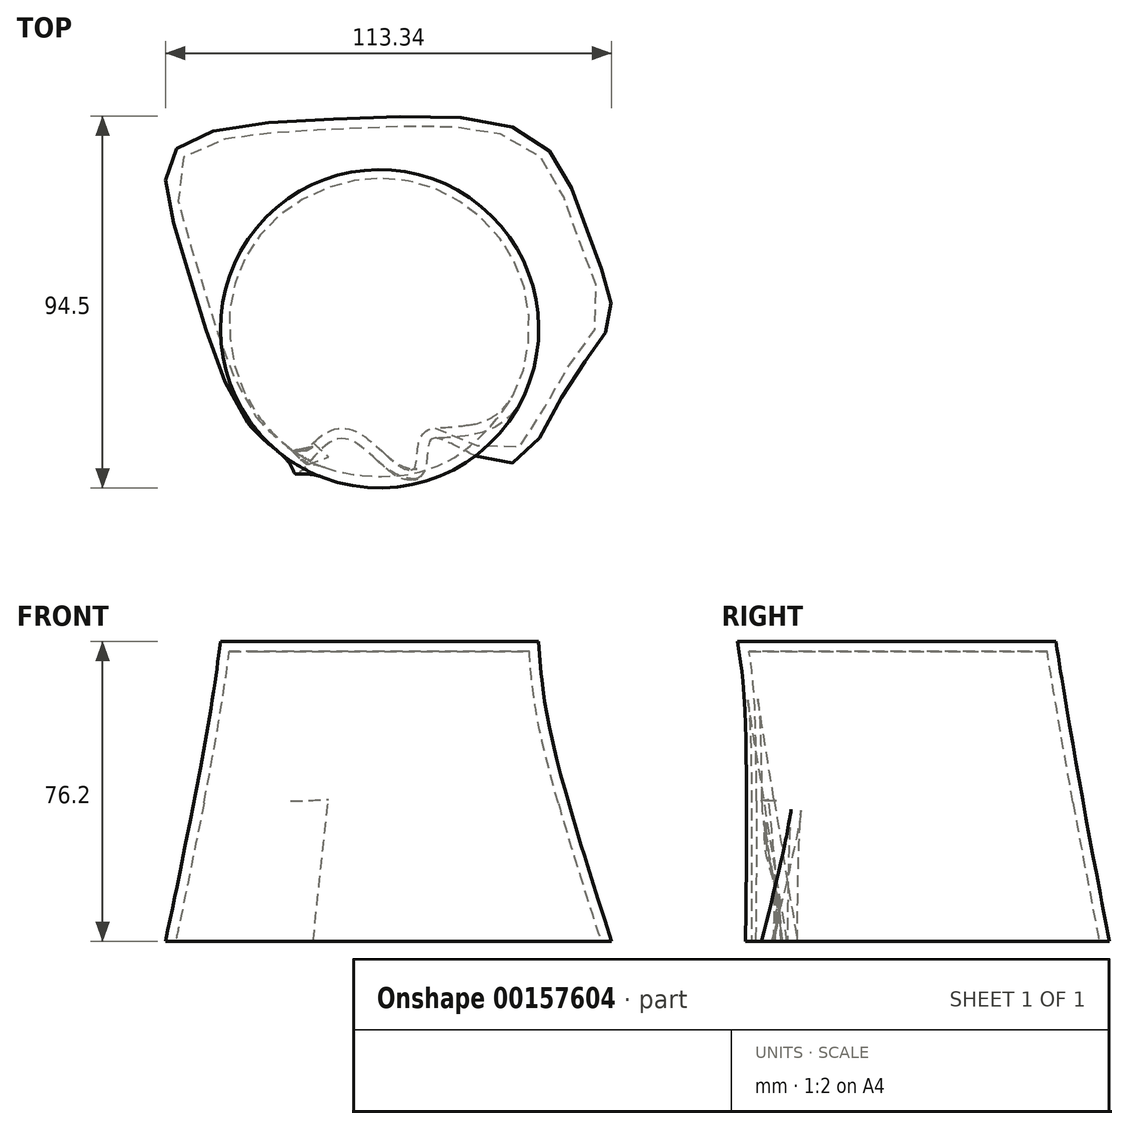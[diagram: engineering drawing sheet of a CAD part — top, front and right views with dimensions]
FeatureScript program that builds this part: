
annotation { "Feature Type Name" : "Feature", "Feature Type Description" : "" }
export const myFeature = defineFeature(function(context is Context, id is Id, definition is map)
    precondition{}
    {
        {
            var Q0;
            Q0=qCreatedBy(makeId("Top.planeOp"),FACE);
            var sketch = newSketch(context, id + "F0", { "sketchPlane" : qUnion([Q0])});
            skFitSpline(sketch, "E0", {"points": [v(-33.5, -23.8) * mm, v(-49.55, 17.73) * mm, v(-52.3, 44.95) * mm, v(-9.4, 53.37) * mm, v(39.96, 48.08) * mm, v(53.67, 22.23) * mm, v(58.76, 2.84) * mm, v(47.8, -14.6) * mm, v(32.12, -34.37) * mm, v(13.51, -27.91) * mm, v(11.36, -36.14) * mm, v(4.5, -37.5) * mm, v(-10.38, -27.91) * mm, v(-20.96, -36.92) * mm, v(-22.72, -34.37) * mm, v(-33.5, -23.8) * mm]});
            skSolve(sketch);
        }
        {
            var Q0;
            Q0=qCreatedBy(makeId("Top.planeOp"),FACE);
            cPlane(context, id + "F1", {"entities" : qUnion([Q0]), "cplaneType" : CPlaneType.OFFSET, "offset" : 76.2 * mm, "width" : 152.4 * mm, "height" : 152.4 * mm});
        }
        {
            var Q0;
            Q0=qCreatedBy(id+"F1.planeOp",FACE);
            var sketch = newSketch(context, id + "F2", { "sketchPlane" : qUnion([Q0])});
            skCircle(sketch, "E1", {"center": v(0, 0) * mm, "radius": 40.44 * mm});
            skSolve(sketch);
        }
        {
            var Q0;
            Q0=makeQuery(id+"F0.imprint","IMPRINT",FACE,{"disambiguationData":[TD([[makeQuery(id+"F0.imprint","IMPRINT",EDGE,{"derivedFrom":sQuery(id+"F0.wireOp",EDGE,"E0")}),-1.0]])]});
            var Q1;
            Q1=makeQuery(id+"F2.imprint","IMPRINT",FACE,{"disambiguationData":[TD([[makeQuery(id+"F2.imprint","IMPRINT",EDGE,{"derivedFrom":sQuery(id+"F2.wireOp",EDGE,"E1")}),1.0]])]});
            loft(context, id + "F3", {"sheetProfilesArray" : [{ "sheetProfileEntities" : qUnion([Q0]) }, { "sheetProfileEntities" : qUnion([Q1]) }]});
        }
        {
            var Q0;
            Q0=makeQuery(id+"F3.opLoft","CAP_FACE",FACE,{"disambiguationData":[OSD([makeQuery(id+"F0.imprint","IMPRINT",FACE,{"disambiguationData":[TD([[makeQuery(id+"F0.imprint","IMPRINT",EDGE,{"derivedFrom":sQuery(id+"F0.wireOp",EDGE,"E0")}),-1.0]])]})])],"isStart":true});
            shell(context, id + "F4", {"entities" : qUnion([Q0]), "thickness" : 2.54 * mm});
        }
    });
